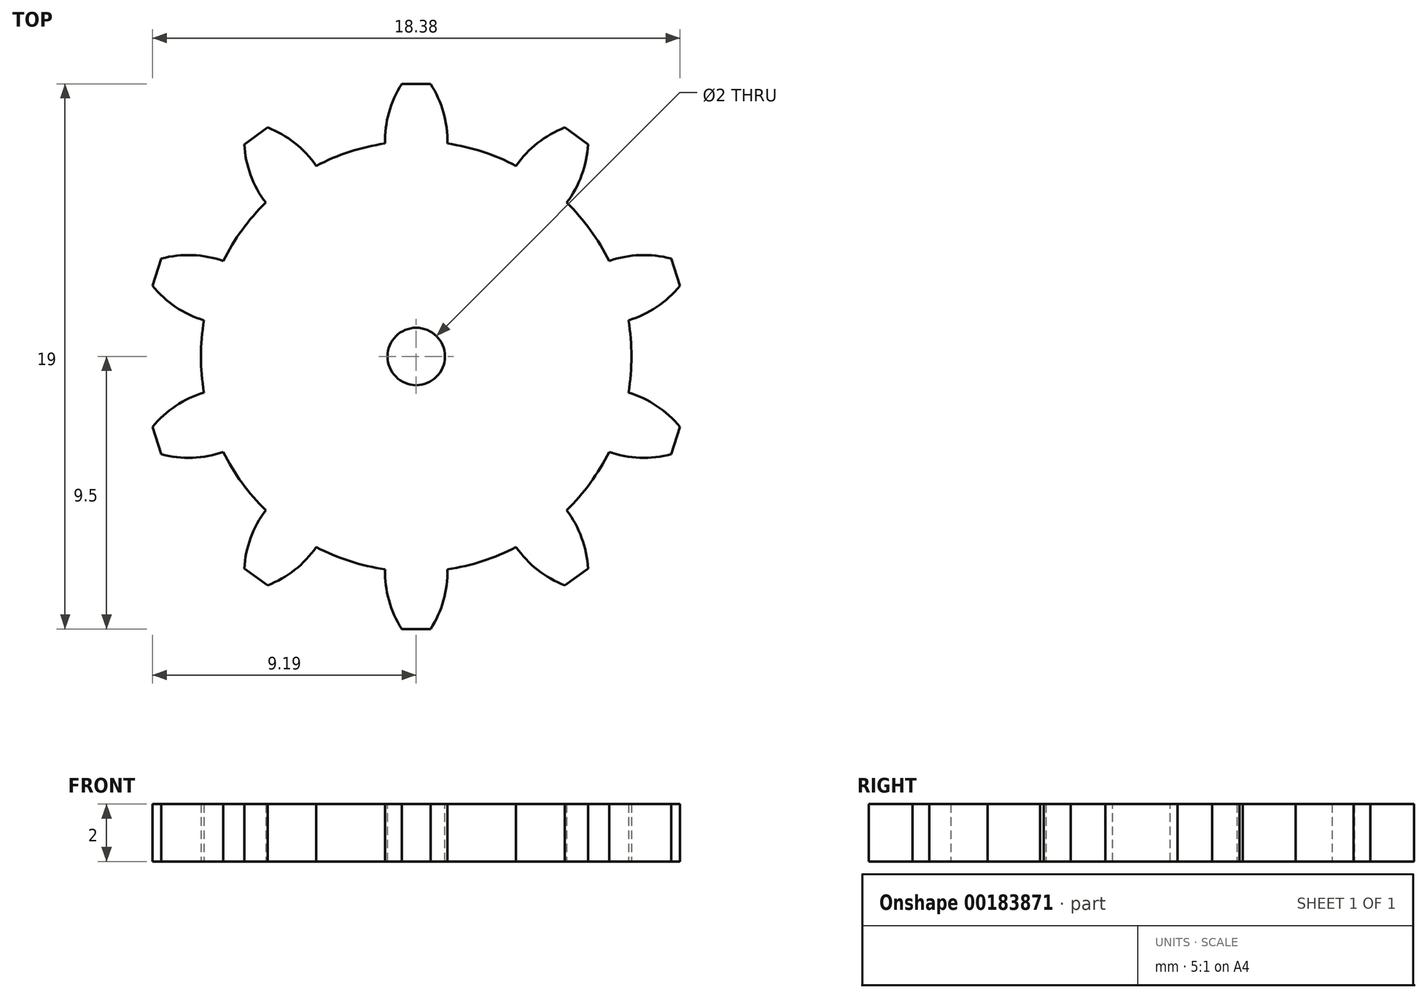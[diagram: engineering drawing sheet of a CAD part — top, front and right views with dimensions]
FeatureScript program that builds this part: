
annotation { "Feature Type Name" : "Feature", "Feature Type Description" : "" }
export const myFeature = defineFeature(function(context is Context, id is Id, definition is map)
    precondition{}
    {
        {
            var Q0;
            Q0=qCreatedBy(makeId("Top.planeOp"),FACE);
            var sketch = newSketch(context, id + "F0", { "sketchPlane" : qUnion([Q0])});
            skCircle(sketch, "E0", {"center": v(0, 0) * mm, "radius": 7.5 * mm});
            skLineSegment(sketch, "E1", {"start": v(0, 0) * mm, "end": v(0, 7.5) * mm, "construction": true});
            skLineSegment(sketch, "E2", {"start": v(0, 9.5) * mm, "end": v(-0.5, 9.5) * mm});
            skArc(sketch, "E3", {"start": v(-0.5, 9.5) * mm, "mid": v(-0.95, 8.5) * mm, "end": v(-1.09, 7.42) * mm});
            skLineSegment(sketch, "E4.MirrorCS", {"start": v(0, 9.5) * mm, "end": v(0.5, 9.5) * mm});
            skArc(sketch, "E5.MirrorCS", {"start": v(0.5, 9.5) * mm, "mid": v(0.95, 8.5) * mm, "end": v(1.09, 7.42) * mm});
            skArc(sketch, "E6.1.0", {"start": v(-5.99, 7.4) * mm, "mid": v(-5.77, 6.32) * mm, "end": v(-5.24, 5.36) * mm});
            skLineSegment(sketch, "E6.1.1", {"start": v(-5.58, 7.69) * mm, "end": v(-5.99, 7.4) * mm});
            skLineSegment(sketch, "E6.1.2", {"start": v(-5.58, 7.69) * mm, "end": v(-5.18, 7.98) * mm});
            skArc(sketch, "E6.1.3", {"start": v(-5.18, 7.98) * mm, "mid": v(-4.23, 7.44) * mm, "end": v(-3.48, 6.64) * mm});
            skArc(sketch, "E6.2.0", {"start": v(-9.19, 2.46) * mm, "mid": v(-8.38, 1.72) * mm, "end": v(-7.4, 1.26) * mm});
            skLineSegment(sketch, "E6.2.1", {"start": v(-9.04, 2.94) * mm, "end": v(-9.19, 2.46) * mm});
            skLineSegment(sketch, "E6.2.2", {"start": v(-9.04, 2.94) * mm, "end": v(-8.88, 3.41) * mm});
            skArc(sketch, "E6.2.3", {"start": v(-8.88, 3.41) * mm, "mid": v(-7.8, 3.53) * mm, "end": v(-6.72, 3.33) * mm});
            skArc(sketch, "E6.3.0", {"start": v(-8.88, -3.41) * mm, "mid": v(-7.8, -3.53) * mm, "end": v(-6.72, -3.33) * mm});
            skLineSegment(sketch, "E6.3.1", {"start": v(-9.04, -2.94) * mm, "end": v(-8.88, -3.41) * mm});
            skLineSegment(sketch, "E6.3.2", {"start": v(-9.04, -2.94) * mm, "end": v(-9.19, -2.46) * mm});
            skArc(sketch, "E6.3.3", {"start": v(-9.19, -2.46) * mm, "mid": v(-8.38, -1.72) * mm, "end": v(-7.4, -1.26) * mm});
            skArc(sketch, "E6.4.0", {"start": v(-5.18, -7.98) * mm, "mid": v(-4.23, -7.44) * mm, "end": v(-3.48, -6.64) * mm});
            skLineSegment(sketch, "E6.4.1", {"start": v(-5.58, -7.69) * mm, "end": v(-5.18, -7.98) * mm});
            skLineSegment(sketch, "E6.4.2", {"start": v(-5.58, -7.69) * mm, "end": v(-5.99, -7.4) * mm});
            skArc(sketch, "E6.4.3", {"start": v(-5.99, -7.4) * mm, "mid": v(-5.77, -6.32) * mm, "end": v(-5.24, -5.36) * mm});
            skArc(sketch, "E6.5.0", {"start": v(0.5, -9.5) * mm, "mid": v(0.95, -8.5) * mm, "end": v(1.09, -7.42) * mm});
            skLineSegment(sketch, "E6.5.1", {"start": v(0, -9.5) * mm, "end": v(0.5, -9.5) * mm});
            skLineSegment(sketch, "E6.5.2", {"start": v(0, -9.5) * mm, "end": v(-0.5, -9.5) * mm});
            skArc(sketch, "E6.5.3", {"start": v(-0.5, -9.5) * mm, "mid": v(-0.95, -8.5) * mm, "end": v(-1.09, -7.42) * mm});
            skArc(sketch, "E6.6.0", {"start": v(5.99, -7.4) * mm, "mid": v(5.77, -6.32) * mm, "end": v(5.24, -5.36) * mm});
            skLineSegment(sketch, "E6.6.1", {"start": v(5.58, -7.69) * mm, "end": v(5.99, -7.4) * mm});
            skLineSegment(sketch, "E6.6.2", {"start": v(5.58, -7.69) * mm, "end": v(5.18, -7.98) * mm});
            skArc(sketch, "E6.6.3", {"start": v(5.18, -7.98) * mm, "mid": v(4.23, -7.44) * mm, "end": v(3.48, -6.64) * mm});
            skArc(sketch, "E6.7.0", {"start": v(9.19, -2.46) * mm, "mid": v(8.38, -1.72) * mm, "end": v(7.4, -1.26) * mm});
            skLineSegment(sketch, "E6.7.1", {"start": v(9.04, -2.94) * mm, "end": v(9.19, -2.46) * mm});
            skLineSegment(sketch, "E6.7.2", {"start": v(9.04, -2.94) * mm, "end": v(8.88, -3.41) * mm});
            skArc(sketch, "E6.7.3", {"start": v(8.88, -3.41) * mm, "mid": v(7.8, -3.53) * mm, "end": v(6.72, -3.33) * mm});
            skArc(sketch, "E6.8.0", {"start": v(8.88, 3.41) * mm, "mid": v(7.8, 3.53) * mm, "end": v(6.72, 3.33) * mm});
            skLineSegment(sketch, "E6.8.1", {"start": v(9.04, 2.94) * mm, "end": v(8.88, 3.41) * mm});
            skLineSegment(sketch, "E6.8.2", {"start": v(9.04, 2.94) * mm, "end": v(9.19, 2.46) * mm});
            skArc(sketch, "E6.8.3", {"start": v(9.19, 2.46) * mm, "mid": v(8.38, 1.72) * mm, "end": v(7.4, 1.26) * mm});
            skArc(sketch, "E6.9.0", {"start": v(5.18, 7.98) * mm, "mid": v(4.23, 7.44) * mm, "end": v(3.48, 6.64) * mm});
            skLineSegment(sketch, "E6.9.1", {"start": v(5.58, 7.69) * mm, "end": v(5.18, 7.98) * mm});
            skLineSegment(sketch, "E6.9.2", {"start": v(5.58, 7.69) * mm, "end": v(5.99, 7.4) * mm});
            skArc(sketch, "E6.9.3", {"start": v(5.99, 7.4) * mm, "mid": v(5.77, 6.32) * mm, "end": v(5.24, 5.36) * mm});
            skSolve(sketch);
        }
        {
            var Q0;
            Q0=qSketchRegion(id+"F0",true);
            extrude(context, id + "F1", {"entities" : qUnion([Q0]), "depth" : 2 * mm});
        }
        {
            var Q0;
            Q0=makeQuery(id+"F1.opExtrude","CAP_FACE",FACE,{"disambiguationData":[OSD([sQuery(id+"F0.wireOp",EDGE,"E0"),sQuery(id+"F0.wireOp",EDGE,"E2"),sQuery(id+"F0.wireOp",EDGE,"E3"),sQuery(id+"F0.wireOp",EDGE,"E4.MirrorCS"),sQuery(id+"F0.wireOp",EDGE,"E5.MirrorCS"),sQuery(id+"F0.wireOp",EDGE,"E6.1.0"),sQuery(id+"F0.wireOp",EDGE,"E6.1.1"),sQuery(id+"F0.wireOp",EDGE,"E6.1.2"),sQuery(id+"F0.wireOp",EDGE,"E6.1.3"),sQuery(id+"F0.wireOp",EDGE,"E6.2.0"),sQuery(id+"F0.wireOp",EDGE,"E6.2.1"),sQuery(id+"F0.wireOp",EDGE,"E6.2.2"),sQuery(id+"F0.wireOp",EDGE,"E6.2.3"),sQuery(id+"F0.wireOp",EDGE,"E6.3.0"),sQuery(id+"F0.wireOp",EDGE,"E6.3.1"),sQuery(id+"F0.wireOp",EDGE,"E6.3.2"),sQuery(id+"F0.wireOp",EDGE,"E6.3.3"),sQuery(id+"F0.wireOp",EDGE,"E6.4.0"),sQuery(id+"F0.wireOp",EDGE,"E6.4.1"),sQuery(id+"F0.wireOp",EDGE,"E6.4.2"),sQuery(id+"F0.wireOp",EDGE,"E6.4.3"),sQuery(id+"F0.wireOp",EDGE,"E6.5.0"),sQuery(id+"F0.wireOp",EDGE,"E6.5.1"),sQuery(id+"F0.wireOp",EDGE,"E6.5.2"),sQuery(id+"F0.wireOp",EDGE,"E6.5.3"),sQuery(id+"F0.wireOp",EDGE,"E6.6.0"),sQuery(id+"F0.wireOp",EDGE,"E6.6.1"),sQuery(id+"F0.wireOp",EDGE,"E6.6.2"),sQuery(id+"F0.wireOp",EDGE,"E6.6.3"),sQuery(id+"F0.wireOp",EDGE,"E6.7.0"),sQuery(id+"F0.wireOp",EDGE,"E6.7.1"),sQuery(id+"F0.wireOp",EDGE,"E6.7.2"),sQuery(id+"F0.wireOp",EDGE,"E6.7.3"),sQuery(id+"F0.wireOp",EDGE,"E6.8.0"),sQuery(id+"F0.wireOp",EDGE,"E6.8.1"),sQuery(id+"F0.wireOp",EDGE,"E6.8.2"),sQuery(id+"F0.wireOp",EDGE,"E6.8.3"),sQuery(id+"F0.wireOp",EDGE,"E6.9.0"),sQuery(id+"F0.wireOp",EDGE,"E6.9.1"),sQuery(id+"F0.wireOp",EDGE,"E6.9.2"),sQuery(id+"F0.wireOp",EDGE,"E6.9.3"),sQuery(id+"F0.wireOp",EDGE,"E6.10.0"),sQuery(id+"F0.wireOp",EDGE,"E6.10.1"),sQuery(id+"F0.wireOp",EDGE,"E6.10.2"),sQuery(id+"F0.wireOp",EDGE,"E6.10.3"),sQuery(id+"F0.wireOp",EDGE,"E6.11.0"),sQuery(id+"F0.wireOp",EDGE,"E6.11.1"),sQuery(id+"F0.wireOp",EDGE,"E6.11.2"),sQuery(id+"F0.wireOp",EDGE,"E6.11.3"),sQuery(id+"F0.wireOp",EDGE,"E6.12.0"),sQuery(id+"F0.wireOp",EDGE,"E6.12.1"),sQuery(id+"F0.wireOp",EDGE,"E6.12.2"),sQuery(id+"F0.wireOp",EDGE,"E6.12.3"),sQuery(id+"F0.wireOp",EDGE,"E6.13.0"),sQuery(id+"F0.wireOp",EDGE,"E6.13.1"),sQuery(id+"F0.wireOp",EDGE,"E6.13.2"),sQuery(id+"F0.wireOp",EDGE,"E6.13.3"),sQuery(id+"F0.wireOp",EDGE,"E6.14.0"),sQuery(id+"F0.wireOp",EDGE,"E6.14.1"),sQuery(id+"F0.wireOp",EDGE,"E6.14.2"),sQuery(id+"F0.wireOp",EDGE,"E6.14.3")])],"isStart":false});
            var sketch = newSketch(context, id + "F2", { "sketchPlane" : qUnion([Q0])});
            skCircle(sketch, "E7", {"center": v(0, 0) * mm, "radius": 1 * mm});
            skSolve(sketch);
        }
        {
            var Q0;
            Q0=makeQuery(id+"F2.imprint","IMPRINT",FACE,{"disambiguationData":[TD([[makeQuery(id+"F2.imprint","IMPRINT",EDGE,{"derivedFrom":sQuery(id+"F2.wireOp",EDGE,"E7")}),1.0]])]});
            extrude(context, id + "F3", {"entities" : qUnion([Q0]), "operationType" : NewBodyOperationType.REMOVE, "endBound" : BoundingType.THROUGH_ALL, "oppositeDirection" : true, "depth" : 25 * mm});
        }
    });
